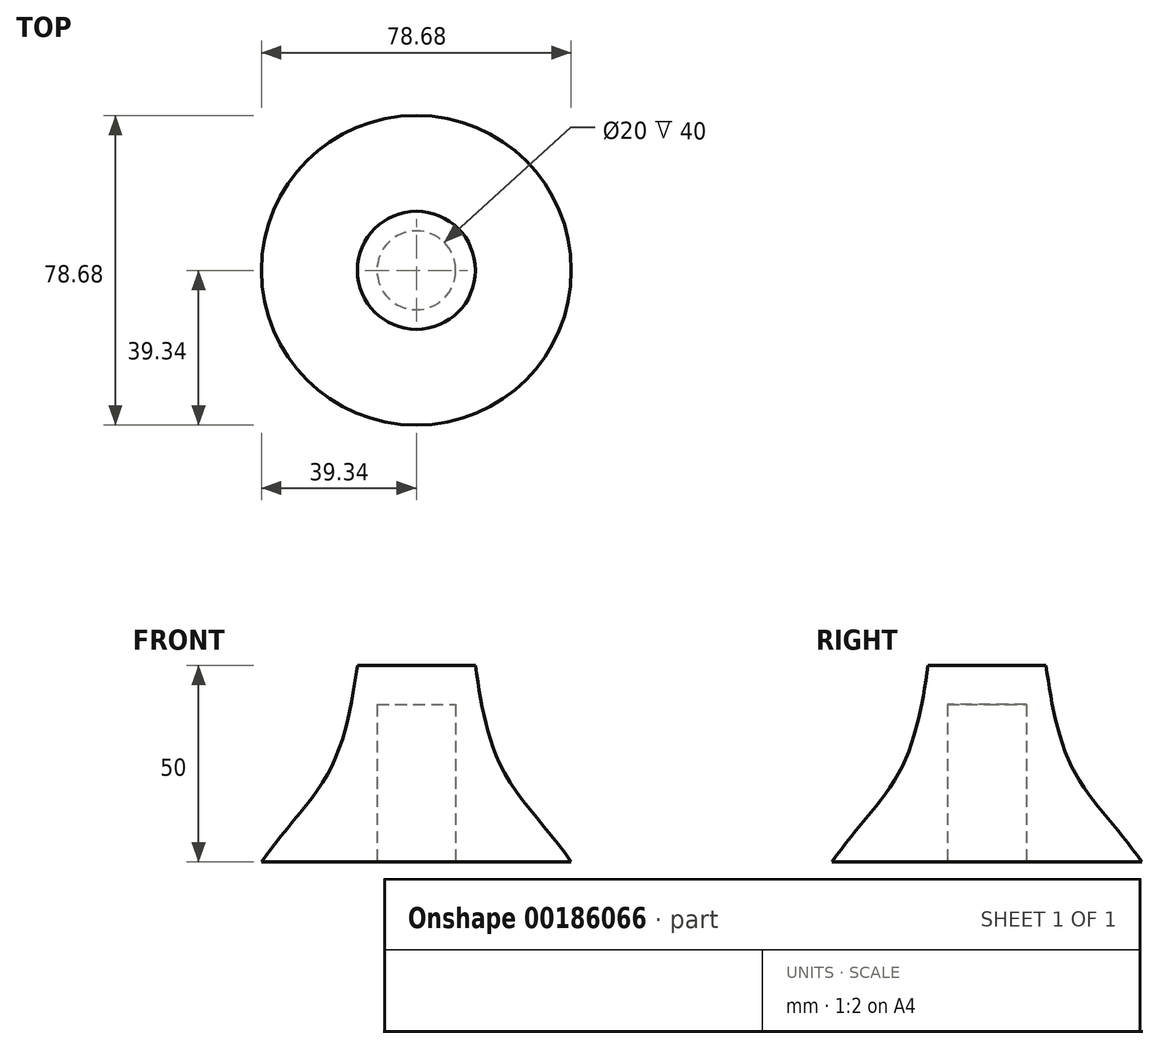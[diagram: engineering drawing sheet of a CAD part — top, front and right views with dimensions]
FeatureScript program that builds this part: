
annotation { "Feature Type Name" : "Feature", "Feature Type Description" : "" }
export const myFeature = defineFeature(function(context is Context, id is Id, definition is map)
    precondition{}
    {
        {
            var Q0;
            Q0=qCreatedBy(makeId("Front.planeOp"),FACE);
            var sketch = newSketch(context, id + "F0", { "sketchPlane" : qUnion([Q0])});
            skLineSegment(sketch, "E0", {"start": v(-39.34, 0) * mm, "end": v(0, 0) * mm});
            skPoint(sketch, "E1", {"position": v(0, 0) * mm});
            skLineSegment(sketch, "E2", {"start": v(0, 0) * mm, "end": v(0, 50) * mm});
            skFitSpline(sketch, "E3", {"points": [v(-15, 50) * mm, v(-21.7, 23.9) * mm, v(-39.34, 0) * mm], "startDerivative": vector(-7.32, -51.57) * mm, "endDerivative": vector(-37.11, -54.23) * mm});
            skLineSegment(sketch, "E4", {"start": v(-15, 50) * mm, "end": v(0, 50) * mm});
            skSolve(sketch);
        }
        {
            var Q0;
            Q0=makeQuery(id+"F0.imprint","IMPRINT",FACE,{"disambiguationData":[TD([[makeQuery(id+"F0.imprint","IMPRINT",EDGE,{"derivedFrom":sQuery(id+"F0.wireOp",EDGE,"E0")}),1.0]])]});
            var Q1;
            Q1=sQuery(id+"F0.wireOp",EDGE,"E2");
            revolve(context, id + "F1", {"entities" : qUnion([Q0]), "axis" : qUnion([Q1]), "revolveType" : RevolveType.FULL});
        }
        {
            var Q0;
            Q0=makeQuery(id+"F1.opRevolve","SWEPT_FACE",FACE,{"disambiguationData":[OSD([sQuery(id+"F0.wireOp",EDGE,"E0")])]});
            var sketch = newSketch(context, id + "F2", { "sketchPlane" : qUnion([Q0])});
            skCircle(sketch, "E5", {"center": v(0, 0) * mm, "radius": 10 * mm});
            skSolve(sketch);
        }
        {
            var Q0;
            Q0=makeQuery(id+"F2.imprint","IMPRINT",FACE,{"disambiguationData":[TD([[makeQuery(id+"F2.imprint","IMPRINT",EDGE,{"derivedFrom":sQuery(id+"F2.wireOp",EDGE,"E5")}),1.0]])]});
            extrude(context, id + "F3", {"entities" : qUnion([Q0]), "operationType" : NewBodyOperationType.REMOVE, "oppositeDirection" : true, "depth" : 40 * mm});
        }
    });
